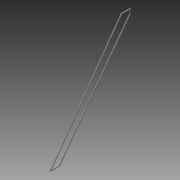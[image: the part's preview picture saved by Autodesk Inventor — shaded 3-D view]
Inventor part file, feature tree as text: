
AUTODESK INVENTOR PART (.ipt)
format: ipt  version: 2015 SP1 (Build 190203100, 203)  size: 80,896 bytes
history: native  units: in
note: dims shown in document units (in); Inventor stores cm internally (conversion verified against a paired STEP export)
features: sketch x2, plane x1, sweep x1
ambient origin geometry x8: Origin, YZ Plane, XZ Plane, XY Plane, X Axis, Y Axis, Z Axis, Center Point
bodies: Body1 (feature_tree)
feature tree (4):
  sketch  "Sketch1"  dims[d0=0.0in d1=0.0in]
  plane  "Work Plane1"
  sweep  "Sweep2"
  sketch  "Sketch3"  dims[d2=1.0in d4=1.0in d5=0.5in d9=0.125in d10=0.0in d11=0.0in]
